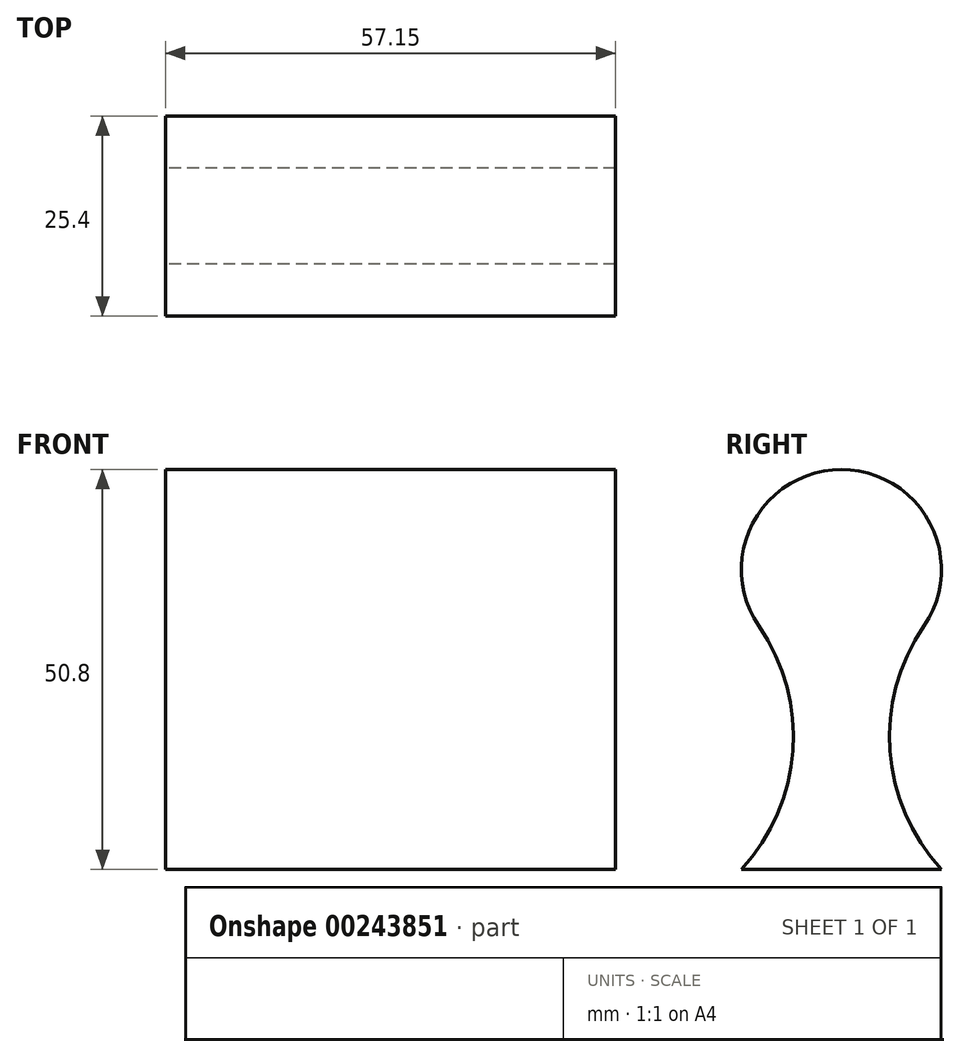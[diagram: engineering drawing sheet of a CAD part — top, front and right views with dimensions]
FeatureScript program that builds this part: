
annotation { "Feature Type Name" : "Feature", "Feature Type Description" : "" }
export const myFeature = defineFeature(function(context is Context, id is Id, definition is map)
    precondition{}
    {
        {
            var Q0;
            Q0=qCreatedBy(makeId("Right.planeOp"),FACE);
            var sketch = newSketch(context, id + "F0", { "sketchPlane" : qUnion([Q0])});
            skLineSegment(sketch, "E0", {"start": v(-12.7, 0) * mm, "end": v(12.7, 0) * mm});
            skLineSegment(sketch, "E1", {"start": v(0, 0) * mm, "end": v(0, 38.1) * mm, "construction": true});
            skArc(sketch, "E2", {"start": v(10.47, 30.91) * mm, "mid": v(0, 50.8) * mm, "end": v(-10.47, 30.91) * mm});
            skArc(sketch, "E3", {"start": v(-12.7, 0) * mm, "mid": v(-6.18, 15.07) * mm, "end": v(-10.47, 30.91) * mm});
            skArc(sketch, "E4.MirrorCS", {"start": v(12.7, 0) * mm, "mid": v(6.18, 15.07) * mm, "end": v(10.47, 30.91) * mm});
            skSolve(sketch);
        }
        {
            var Q0;
            Q0 = qSketchRegion(id + "F0", true);
            extrude(context, id + "F1", {"entities" : qUnion([Q0]), "depth" : 57.15 * mm, "offsetDistance" : 25.4 * mm});
        }
    });
